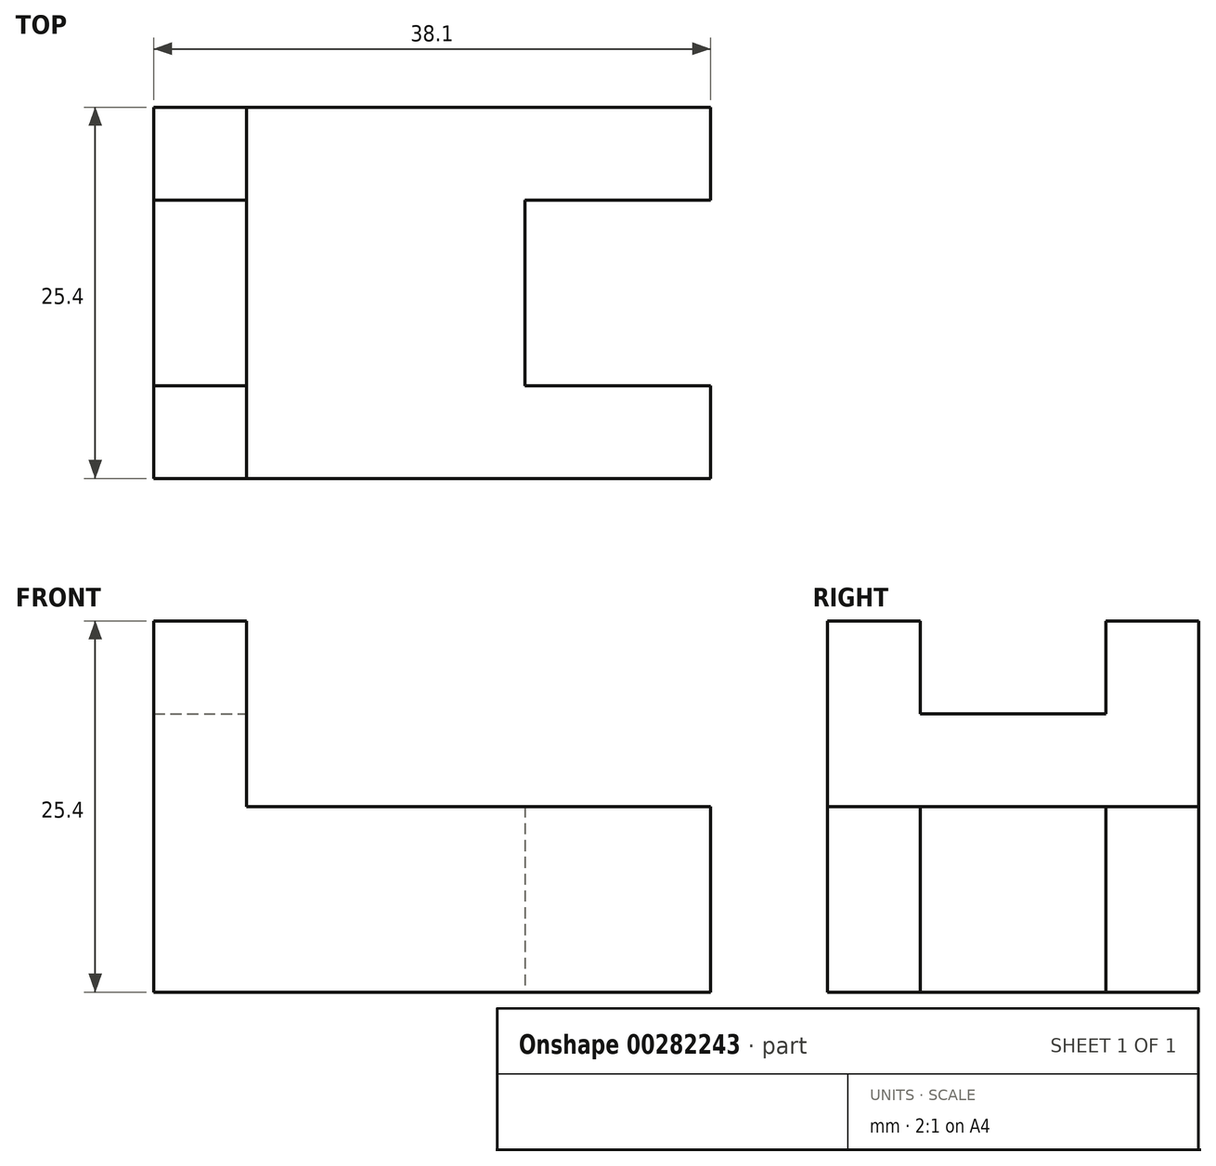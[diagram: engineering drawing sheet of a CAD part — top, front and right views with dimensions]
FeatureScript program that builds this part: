
annotation { "Feature Type Name" : "Feature", "Feature Type Description" : "" }
export const myFeature = defineFeature(function(context is Context, id is Id, definition is map)
    precondition{}
    {
        {
            var Q0;
            Q0=qCreatedBy(makeId("Front.planeOp"),FACE);
            var sketch = newSketch(context, id + "F0", { "sketchPlane" : qUnion([Q0])});
            skLineSegment(sketch, "E0", {"start": v(0, 0) * mm, "end": v(0, 25.4) * mm});
            skLineSegment(sketch, "E1", {"start": v(0, 0) * mm, "end": v(38.1, 0) * mm});
            skLineSegment(sketch, "E2", {"start": v(38.1, 0) * mm, "end": v(38.1, 12.7) * mm});
            skLineSegment(sketch, "E3", {"start": v(38.1, 12.7) * mm, "end": v(6.35, 12.7) * mm});
            skLineSegment(sketch, "E4", {"start": v(6.35, 12.7) * mm, "end": v(6.35, 25.4) * mm});
            skLineSegment(sketch, "E5", {"start": v(6.35, 25.4) * mm, "end": v(0, 25.4) * mm});
            skSolve(sketch);
        }
        {
            var Q0;
            Q0=makeQuery(id+"F0.imprint","IMPRINT",FACE,{"disambiguationData":[TD([[makeQuery(id+"F0.imprint","IMPRINT",EDGE,{"derivedFrom":sQuery(id+"F0.wireOp",EDGE,"E0")}),-1.0]])]});
            extrude(context, id + "F1", {"entities" : qUnion([Q0]), "endBound" : BoundingType.SYMMETRIC, "depth" : 25.4 * mm});
        }
        {
            var Q0;
            Q0=qCreatedBy(makeId("Front.planeOp"),FACE);
            var sketch = newSketch(context, id + "F2", { "sketchPlane" : qUnion([Q0])});
            skLineSegment(sketch, "E6.bottom", {"start": v(0, 25.4) * mm, "end": v(6.35, 25.4) * mm});
            skLineSegment(sketch, "E6.top", {"start": v(0, 19.05) * mm, "end": v(6.35, 19.05) * mm});
            skLineSegment(sketch, "E6.left", {"start": v(0, 25.4) * mm, "end": v(0, 19.05) * mm});
            skLineSegment(sketch, "E6.right", {"start": v(6.35, 25.4) * mm, "end": v(6.35, 19.05) * mm});
            skSolve(sketch);
        }
        {
            var Q0;
            Q0 = qSketchRegion(id + "F2", true);
            extrude(context, id + "F3", {"entities" : qUnion([Q0]), "operationType" : NewBodyOperationType.REMOVE, "endBound" : BoundingType.SYMMETRIC, "depth" : 12.7 * mm});
        }
        {
            var Q0;
            Q0=qCreatedBy(makeId("Front.planeOp"),FACE);
            var sketch = newSketch(context, id + "F4", { "sketchPlane" : qUnion([Q0])});
            skLineSegment(sketch, "E7.bottom", {"start": v(25.4, 12.7) * mm, "end": v(38.1, 12.7) * mm});
            skLineSegment(sketch, "E7.top", {"start": v(25.4, 0) * mm, "end": v(38.1, 0) * mm});
            skLineSegment(sketch, "E7.left", {"start": v(25.4, 12.7) * mm, "end": v(25.4, 0) * mm});
            skLineSegment(sketch, "E7.right", {"start": v(38.1, 12.7) * mm, "end": v(38.1, 0) * mm});
            skSolve(sketch);
        }
        {
            var Q0;
            Q0 = qSketchRegion(id + "F4", true);
            extrude(context, id + "F5", {"entities" : qUnion([Q0]), "operationType" : NewBodyOperationType.REMOVE, "endBound" : BoundingType.SYMMETRIC, "depth" : 12.7 * mm});
        }
    });
